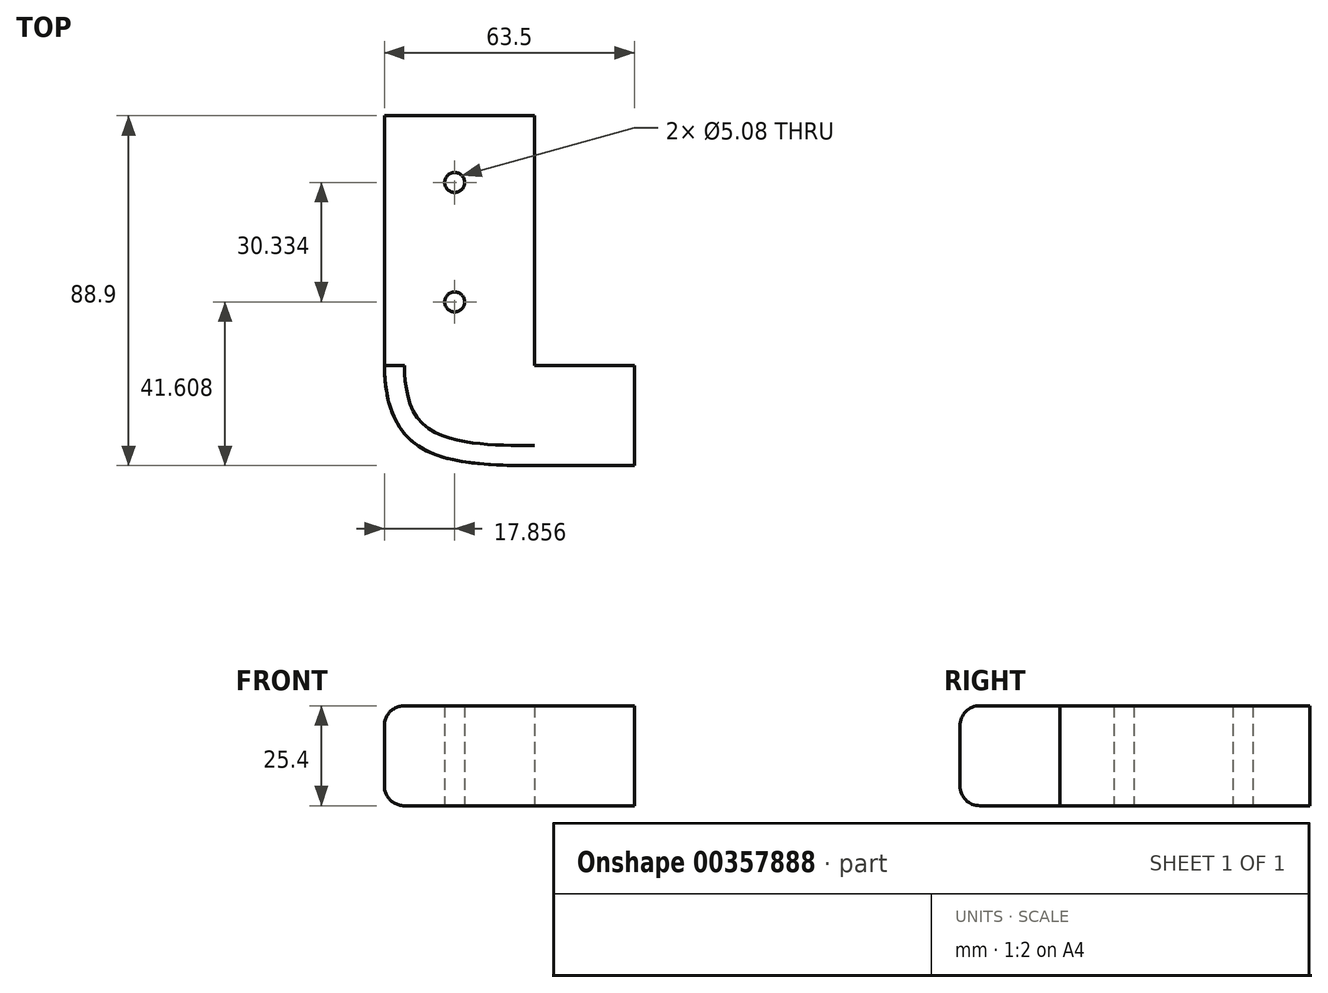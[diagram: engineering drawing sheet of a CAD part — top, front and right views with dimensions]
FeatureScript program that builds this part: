
annotation { "Feature Type Name" : "Feature", "Feature Type Description" : "" }
export const myFeature = defineFeature(function(context is Context, id is Id, definition is map)
    precondition{}
    {
        {
            var Q0;
            Q0=qCreatedBy(makeId("Top.planeOp"),FACE);
            var sketch = newSketch(context, id + "F0", { "sketchPlane" : qUnion([Q0])});
            skLineSegment(sketch, "E0.bottom", {"start": v(0, 0) * mm, "end": v(-38.1, 0) * mm});
            skLineSegment(sketch, "E0.top", {"start": v(0, 63.5) * mm, "end": v(-38.1, 63.5) * mm});
            skLineSegment(sketch, "E0.left", {"start": v(0, 0) * mm, "end": v(0, 63.5) * mm});
            skLineSegment(sketch, "E0.right", {"start": v(-38.1, 0) * mm, "end": v(-38.1, 63.5) * mm});
            skLineSegment(sketch, "E1.bottom", {"start": v(0, 0) * mm, "end": v(25.4, 0) * mm});
            skLineSegment(sketch, "E1.top", {"start": v(0, -25.4) * mm, "end": v(25.4, -25.4) * mm});
            skLineSegment(sketch, "E1.left", {"start": v(0, 0) * mm, "end": v(0, -25.4) * mm});
            skLineSegment(sketch, "E1.right", {"start": v(25.4, 0) * mm, "end": v(25.4, -25.4) * mm});
            skFitSpline(sketch, "E2", {"points": [v(-38.1, 0) * mm, v(0, -25.4) * mm], "startDerivative": vector(1.26, -68.53) * mm, "endDerivative": vector(72.93, 0) * mm});
            skCircle(sketch, "E3", {"center": v(-20.24, 46.54) * mm, "radius": 2.54 * mm});
            skCircle(sketch, "E4", {"center": v(-20.24, 16.2) * mm, "radius": 2.54 * mm});
            skSolve(sketch);
        }
        {
            var Q0;
            Q0=makeQuery(id+"F0.imprint","IMPRINT",FACE,{"disambiguationData":[TD([[makeQuery(id+"F0.imprint","IMPRINT",EDGE,{"derivedFrom":sQuery(id+"F0.wireOp",EDGE,"E0.bottom")}),-1.0]])]});
            var Q1;
            Q1=makeQuery(id+"F0.imprint","IMPRINT",FACE,{"disambiguationData":[TD([[makeQuery(id+"F0.imprint","IMPRINT",EDGE,{"derivedFrom":sQuery(id+"F0.wireOp",EDGE,"E1.bottom")}),-1.0]])]});
            var Q2;
            Q2=makeQuery(id+"F0.imprint","IMPRINT",FACE,{"disambiguationData":[TD([[makeQuery(id+"F0.imprint","IMPRINT",EDGE,{"derivedFrom":sQuery(id+"F0.wireOp",EDGE,"E0.bottom")}),1.0]])]});
            extrude(context, id + "F1", {"entities" : qUnion([Q0, Q1, Q2]), "depth" : 25.4 * mm});
        }
        {
            var Q0;
            Q0=makeQuery(id+"F1.opExtrude","CAP_EDGE",EDGE,{"disambiguationData":[OSD([sQuery(id+"F0.wireOp",EDGE,"E0.right")])],"isStart":false});
            var Q1;
            Q1=makeQuery(id+"F1.opExtrude","CAP_EDGE",EDGE,{"disambiguationData":[OSD([sQuery(id+"F0.wireOp",EDGE,"E0.right")])],"isStart":true});
            var Q2;
            Q2=makeQuery(id+"F1.opExtrude","CAP_EDGE",EDGE,{"disambiguationData":[OSD([sQuery(id+"F0.wireOp",EDGE,"E2")])],"isStart":false});
            var Q3;
            Q3=makeQuery(id+"F1.opExtrude","CAP_EDGE",EDGE,{"disambiguationData":[OSD([sQuery(id+"F0.wireOp",EDGE,"E2")])],"isStart":true});
            fillet(context, id + "F2", {"entities" : qUnion([Q0, Q1, Q2, Q3]), "radius" : 5.08 * mm, "tangentPropagation" : true, "allowEdgeOverflow" : false});
        }
    });
